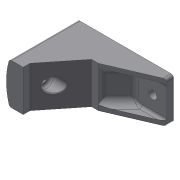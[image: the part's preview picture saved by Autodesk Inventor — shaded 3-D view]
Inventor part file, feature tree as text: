
AUTODESK INVENTOR PART (.ipt)
format: ipt  version: 2018 (Build 220112000, 112)  size: 230,912 bytes
history: native  units: mm
features: sketch x7, extrude x5, fillet x5, projected_geometry x5, hole x2, chamfer x2, mirror x1
ambient origin geometry x8: Origin, YZ Plane, XZ Plane, XY Plane, X Axis, Y Axis, Z Axis, Center Point
bodies: Solid1 (feature_tree)
feature tree (27):
  extrude  "Extrusion1"  Depth=30.0mm
  extrude  "Extrusion2"  Depth=50.0mm
  extrude  "Extrusion3"  Depth=30.0mm TaperAngle=0.0deg
  hole  "Hole1"  [1 undecoded]
  extrude  "Extrusion4"  Depth=2.0mm TaperAngle=0.0deg
  mirror  "Mirror1"
  chamfer  "Chamfer1"  Distance=2.0mm Angle=45.0deg
  fillet  "Fillet1"  Radius=5.0mm
  chamfer  "Chamfer2"  Distance=25.0mm Angle=45.0deg
  extrude  "Extrusion5"  Depth=10.0mm
  fillet  "Fillet2"  Radius=60.0mm
  fillet  "Fillet3"  Radius=0.5mm
  hole  "Hole2"  [1 undecoded]
  fillet  "Fillet4"  Radius=2.0mm
  fillet  "Fillet5"  Radius=2.0mm
  sketch  "Sketch1"  dims[d0=100.0mm d1=30.0mm]
  sketch  "Sketch2"  dims[d2=50.0mm d3=0.0mm d4=70.0mm]
  projected_geometry  "Projected Loop1"
  sketch  "Sketch3"  dims[d5=60.0mm d6=30.0mm d7=0.0mm]
  projected_geometry  "Projected Loop2"
  sketch  "Sketch4"  dims[d8=35.0mm d9=15.0mm d10=0.0mm]
  sketch  "Sketch5"  dims[d11=12.0mm]
  projected_geometry  "Projected Loop3"
  sketch  "Sketch6"  dims[d12=6.0mm d13=6.0mm d14=3.023mm d15=2.0mm d16=14.3117mm d17=8.0mm d18=20.594885mm d19=3.0mm d20=0.0mm d21=12.0mm d22=2.0mm d23=45.0deg d24=5.0mm d25=25.0mm d26=20.0mm d27=45.0deg]
  projected_geometry  "Projected Loop4"
  sketch  "Sketch7"  dims[d28=15.0mm d29=10.0mm d30=60.0mm d31=0.0mm d32=0.5mm d33=2.0mm d34=4.3mm d35=9.0mm d36=9.4mm d37=2.0mm d38=90.0deg d39=8.0mm d40=20.594885mm d41=2.0mm d42=2.0mm]
  projected_geometry  "Projected Loop5"
note: 2 required parameter values undecoded (feature->parameter linkage not recoverable at this tier; creation-order binding heuristic only, values carry confidence <= 0.55)
